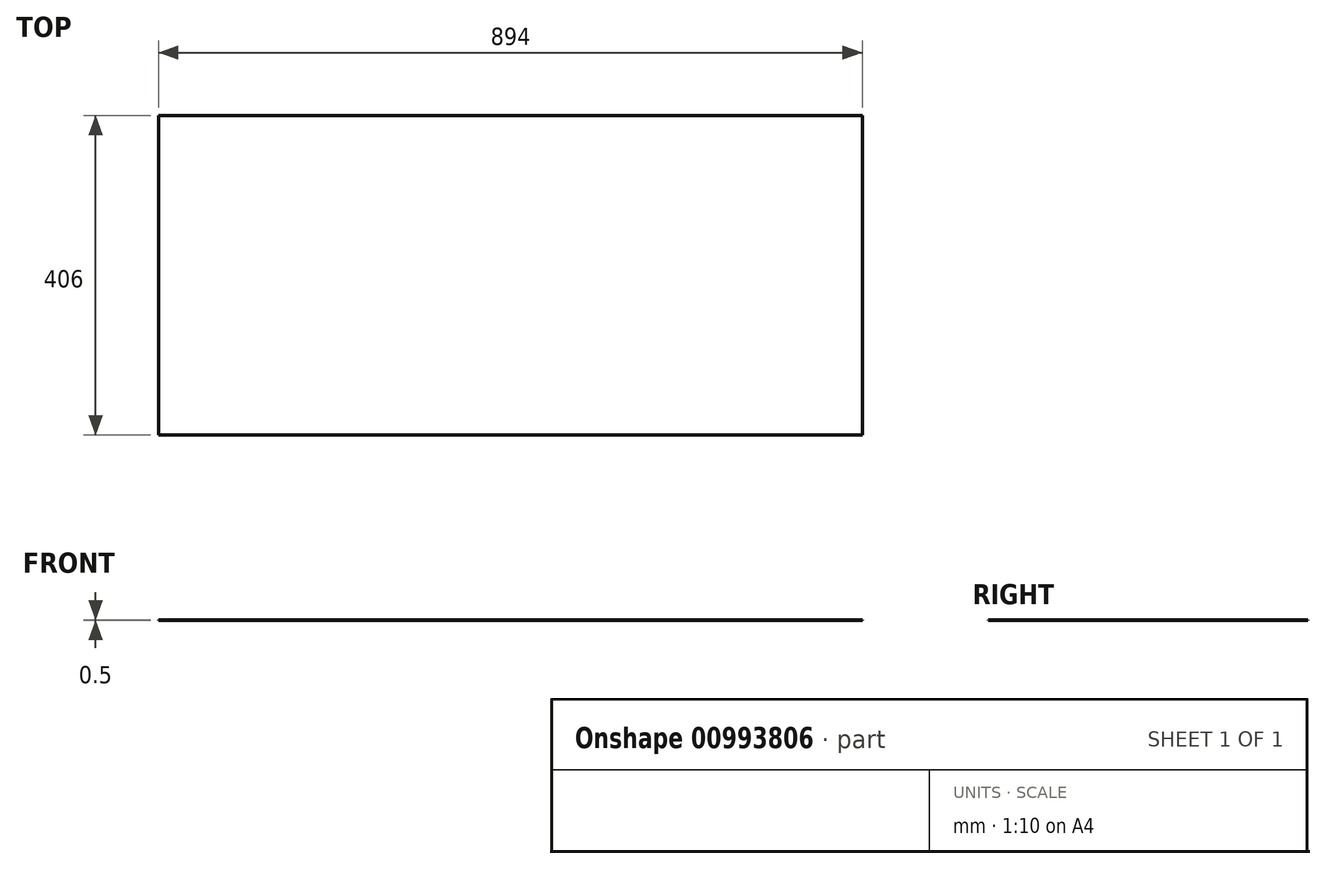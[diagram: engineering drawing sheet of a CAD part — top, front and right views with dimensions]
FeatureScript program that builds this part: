
annotation { "Feature Type Name" : "Feature", "Feature Type Description" : "" }
export const myFeature = defineFeature(function(context is Context, id is Id, definition is map)
    precondition{}
    {
        {
            var Q0;
            Q0=qCreatedBy(makeId("Top.planeOp"),FACE);
            var sketch = newSketch(context, id + "F0", { "sketchPlane" : qUnion([Q0])});
            skLineSegment(sketch, "E0.bottom", {"start": v(447, 203) * mm, "end": v(-447, 203) * mm});
            skLineSegment(sketch, "E0.top", {"start": v(447, -203) * mm, "end": v(-447, -203) * mm});
            skLineSegment(sketch, "E0.left", {"start": v(447, 203) * mm, "end": v(447, -203) * mm});
            skLineSegment(sketch, "E0.right", {"start": v(-447, 203) * mm, "end": v(-447, -203) * mm});
            skPoint(sketch, "E0.middle", {"position": v(0, 0) * mm});
            skSolve(sketch);
        }
        {
            var Q0;
            Q0=makeQuery(id+"F0.imprint","IMPRINT",FACE,{"disambiguationData":[TD([[makeQuery(id+"F0.imprint","IMPRINT",EDGE,{"derivedFrom":sQuery(id+"F0.wireOp",EDGE,"E0.bottom")}),1.0]])]});
            extrude(context, id + "F1", {"entities" : qUnion([Q0]), "depth" : 0.5 * mm, "offsetDistance" : 25 * mm});
        }
    });
